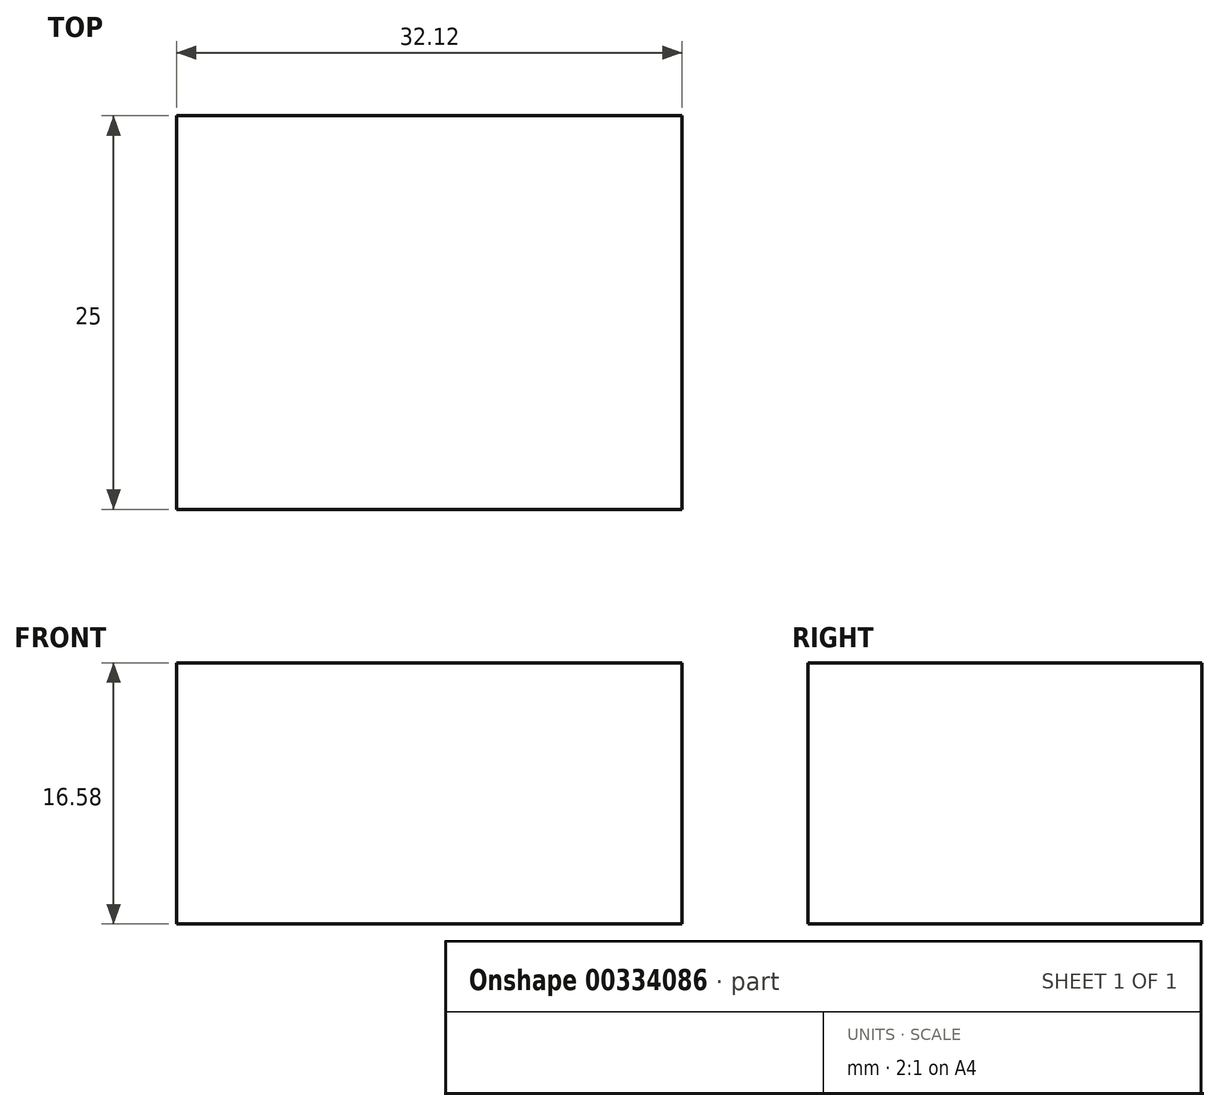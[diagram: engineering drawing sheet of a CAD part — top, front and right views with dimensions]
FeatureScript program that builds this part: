
annotation { "Feature Type Name" : "Feature", "Feature Type Description" : "" }
export const myFeature = defineFeature(function(context is Context, id is Id, definition is map)
    precondition{}
    {
        {
            var Q0;
            Q0=qCreatedBy(makeId("Front.planeOp"),FACE);
            var sketch = newSketch(context, id + "F0", { "sketchPlane" : qUnion([Q0])});
            skLineSegment(sketch, "E0.bottom", {"start": v(-59.73, 45.36) * mm, "end": v(-91.85, 45.36) * mm});
            skLineSegment(sketch, "E0.top", {"start": v(-59.73, 61.94) * mm, "end": v(-91.85, 61.94) * mm});
            skLineSegment(sketch, "E0.left", {"start": v(-59.73, 45.36) * mm, "end": v(-59.73, 61.94) * mm});
            skLineSegment(sketch, "E0.right", {"start": v(-91.85, 45.36) * mm, "end": v(-91.85, 61.94) * mm});
            skPoint(sketch, "E0.middle", {"position": v(-75.8, 53.65) * mm});
            skSolve(sketch);
        }
        {
            var Q0;
            Q0 = qSketchRegion(id + "F0", true);
            extrude(context, id + "F1", {"entities" : qUnion([Q0]), "depth" : 25 * mm});
        }
    });
